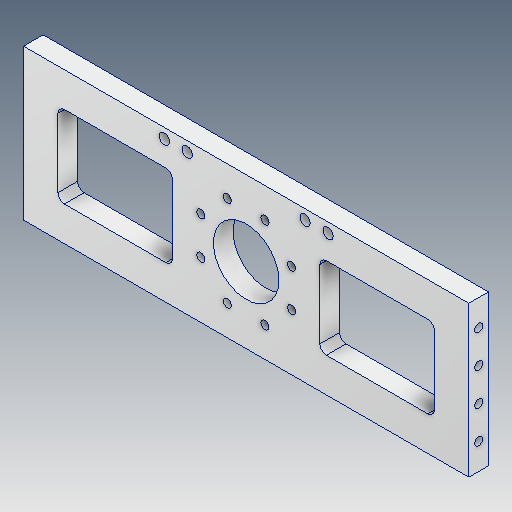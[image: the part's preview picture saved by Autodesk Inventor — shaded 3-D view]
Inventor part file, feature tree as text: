
AUTODESK INVENTOR PART (.ipt)
format: ipt  version: 2020.5 (Build 245400000, 400)  size: 246,784 bytes
history: native  units: mm
features: extrude x7, sketch x7, other x1, projected_geometry x1
ambient origin geometry x8: Origin, YZ Plane, XZ Plane, XY Plane, X Axis, Y Axis, Z Axis, Center Point
bodies: Body1 (feature_tree)
feature tree (16):
  other  "솔리드1"
  extrude  "돌출1"  Depth=46.0mm
  extrude  "돌출2"  Depth=136.0mm
  extrude  "돌출3"  Depth=6.0mm TaperAngle=0.0deg
  extrude  "돌출4"  Depth=6.0mm TaperAngle=0.0deg
  extrude  "돌출5"  Depth=20.0mm
  extrude  "돌출6"  Depth=6.0mm TaperAngle=0.0deg
  extrude  "돌출8"  Depth=2.5mm
  sketch  "스케치1"
  sketch  "스케치2"
  sketch  "스케치3"
  sketch  "스케치4"
  sketch  "스케치5"
  sketch  "스케치6"
  projected_geometry  "투영된 루프1"
  sketch  "스케치11"
